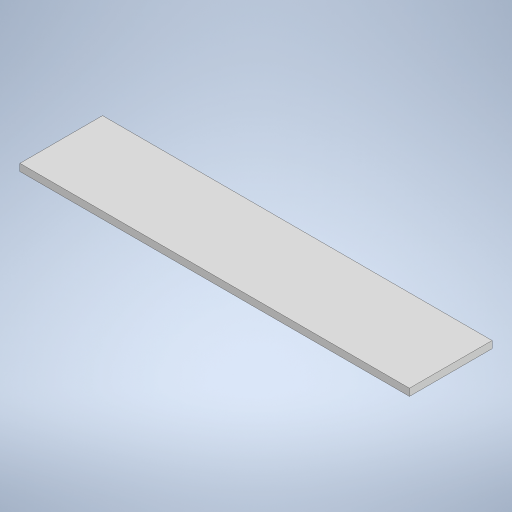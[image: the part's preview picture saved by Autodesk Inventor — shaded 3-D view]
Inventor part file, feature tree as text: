
AUTODESK INVENTOR PART (.ipt)
format: ipt  version: 2023 (Build 270158000, 158)  size: 215,552 bytes
history: native  units: mm
features: extrude x1, sketch x1
ambient origin geometry x8: Origin, YZ Plane, XZ Plane, XY Plane, X Axis, Y Axis, Z Axis, Center Point
bodies: Solid1 (feature_tree)
feature tree (2):
  extrude  "Extrusion1"  Depth=165.0mm
  sketch  "Sketch1"  dims[d0=35.0mm d1=165.0mm d2=3.0mm d3=0.0mm]
